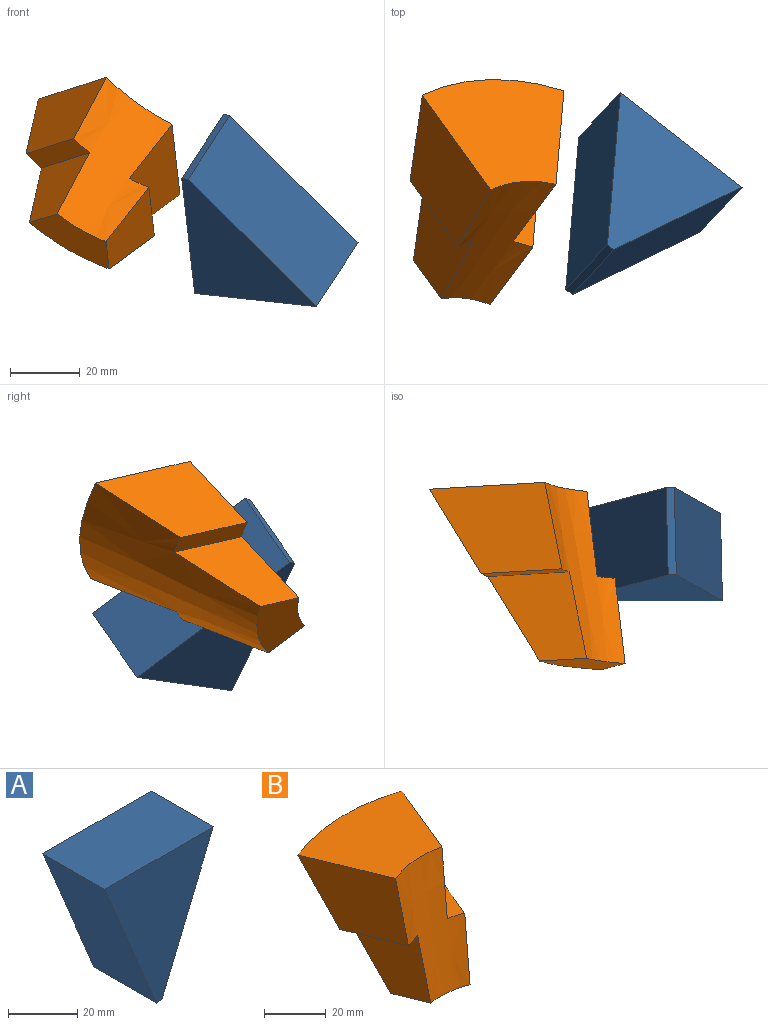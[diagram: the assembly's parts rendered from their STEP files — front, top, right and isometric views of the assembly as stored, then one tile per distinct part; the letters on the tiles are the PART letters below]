
ASSEMBLY  parts=2 mates=2
PART A: 6 faces, bbox 44.5x25.4x50.8 mm
  f0: plane 25.4x2.37mm, normal (0,0,-1), area 60.1mm2, adj f1,f2,f4,f5
  f1: plane 50.8x44.45mm, normal (0,-1,0), area 1189.1mm2, adj f0,f3,f4,f5
  f2: plane 50.8x44.45mm, normal (0,1,0), area 1189.1mm2, adj f0,f3,f4,f5
  f3: plane 44.45x25.4mm, normal (0,0,1), area 1129mm2, adj f1,f2,f4,f5
  f4: plane 50.8x25.4mm, normal (-0.92,0,-0.38), area 1396.6mm2, adj f0,f1,f2,f3
  f5: plane 50.8x25.4mm, normal (0.92,0,-0.38), area 1396.6mm2, adj f0,f1,f2,f3
PART B: 10 faces, bbox 56.4x45.4x51.1 mm
  f0: plane 26.48x15.77mm, normal (0,0,-1), area 292.4mm2, adj f3,f7,f8,f9
  f1: plane 35.64x25.4mm, normal (-0.92,-0.38,0), area 736.8mm2, adj f2,f6,f8,f9
  f2: plane 49.07x36.82mm, normal (0,0,1), area 1250.5mm2, adj f1,f5,f8,f9
  f3: plane 25.65x25.48mm, normal (0.92,-0.38,0), area 459.9mm2, adj f0,f4,f8,f9
  f4: plane 23.71x14.98mm, normal (0,0,1), area 148.4mm2, adj f3,f5,f8,f9
  f5: plane 35.55x25.53mm, normal (0.92,-0.38,0), area 729.3mm2, adj f2,f4,f8,f9
  f6: plane 24.19x15.25mm, normal (0,0,-1), area 152.4mm2, adj f1,f7,f8,f9
  f7: plane 26.85x25.71mm, normal (-0.92,-0.38,0), area 483.8mm2, adj f0,f6,f8,f9
  f8: cone r=69.85mm half-angle=30deg, axis (0,0,1), area 2263.3mm2, adj f0,f1,f2,f3,f4,f5,f6,f7
  f9: cone r=38.1mm half-angle=10deg, axis (0,0,1), area 1031.5mm2, adj f0,f1,f2,f3,f4,f5,f6,f7
PLACE A rot(axis=(0.32,0.87,0.39),169.6deg) t=(33.67,-38.27,46.63)mm
PLACE B rot(axis=(-0.66,0.72,0.19),44.6deg) t=(-68.04,2,14.42)mm
MATE parallel B.f5 <-> A.f5  axis (0.88,-0.33,-0.34) through (-4.32,-2.74,29.88)mm
MATE parallel B.f2 <-> A.f2  axis (0.47,0.5,0.72) through (-14.49,9.69,44.38)mm
